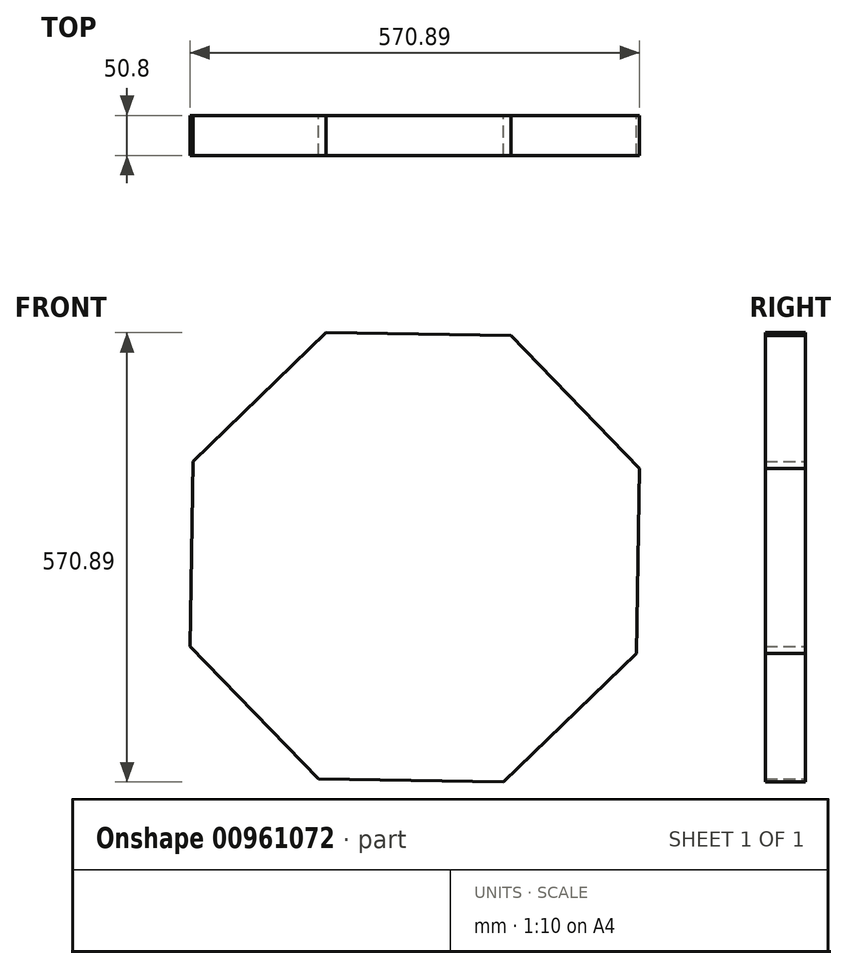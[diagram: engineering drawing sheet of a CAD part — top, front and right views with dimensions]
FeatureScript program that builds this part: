
annotation { "Feature Type Name" : "Feature", "Feature Type Description" : "" }
export const myFeature = defineFeature(function(context is Context, id is Id, definition is map)
    precondition{}
    {
        {
            var Q0;
            Q0=qCreatedBy(makeId("Front.planeOp"),FACE);
            var sketch = newSketch(context, id + "F0", { "sketchPlane" : qUnion([Q0])});
            skCircle(sketch, "E0.cCircle", {"center": v(-0.46, 8.8) * mm, "radius": 283.6 * mm, "construction": true});
            skLineSegment(sketch, "E0.0", {"start": v(112.48, -276.65) * mm, "end": v(-122.44, -272.9) * mm});
            skLineSegment(sketch, "E0.1", {"start": v(-122.44, -272.9) * mm, "end": v(-285.9, -104.15) * mm});
            skLineSegment(sketch, "E0.2", {"start": v(-285.9, -104.15) * mm, "end": v(-282.16, 130.77) * mm});
            skLineSegment(sketch, "E0.3", {"start": v(-282.16, 130.77) * mm, "end": v(-113.4, 294.24) * mm});
            skLineSegment(sketch, "E0.4", {"start": v(-113.4, 294.24) * mm, "end": v(121.52, 290.5) * mm});
            skLineSegment(sketch, "E0.5", {"start": v(121.52, 290.5) * mm, "end": v(284.98, 121.74) * mm});
            skLineSegment(sketch, "E0.6", {"start": v(284.98, 121.74) * mm, "end": v(281.24, -113.18) * mm});
            skLineSegment(sketch, "E0.7", {"start": v(281.24, -113.18) * mm, "end": v(112.48, -276.65) * mm});
            skPoint(sketch, "E0.0.midPoint", {"position": v(-4.98, -274.78) * mm});
            skSolve(sketch);
        }
        {
            var Q0;
            Q0=makeQuery(id+"F0.imprint","IMPRINT",FACE,{"disambiguationData":[TD([[makeQuery(id+"F0.imprint","IMPRINT",EDGE,{"derivedFrom":sQuery(id+"F0.wireOp",EDGE,"E0.0")}),-1.0]])]});
            extrude(context, id + "F1", {"entities" : qUnion([Q0]), "depth" : 50.8 * mm, "offsetDistance" : 25.4 * mm});
        }
    });
